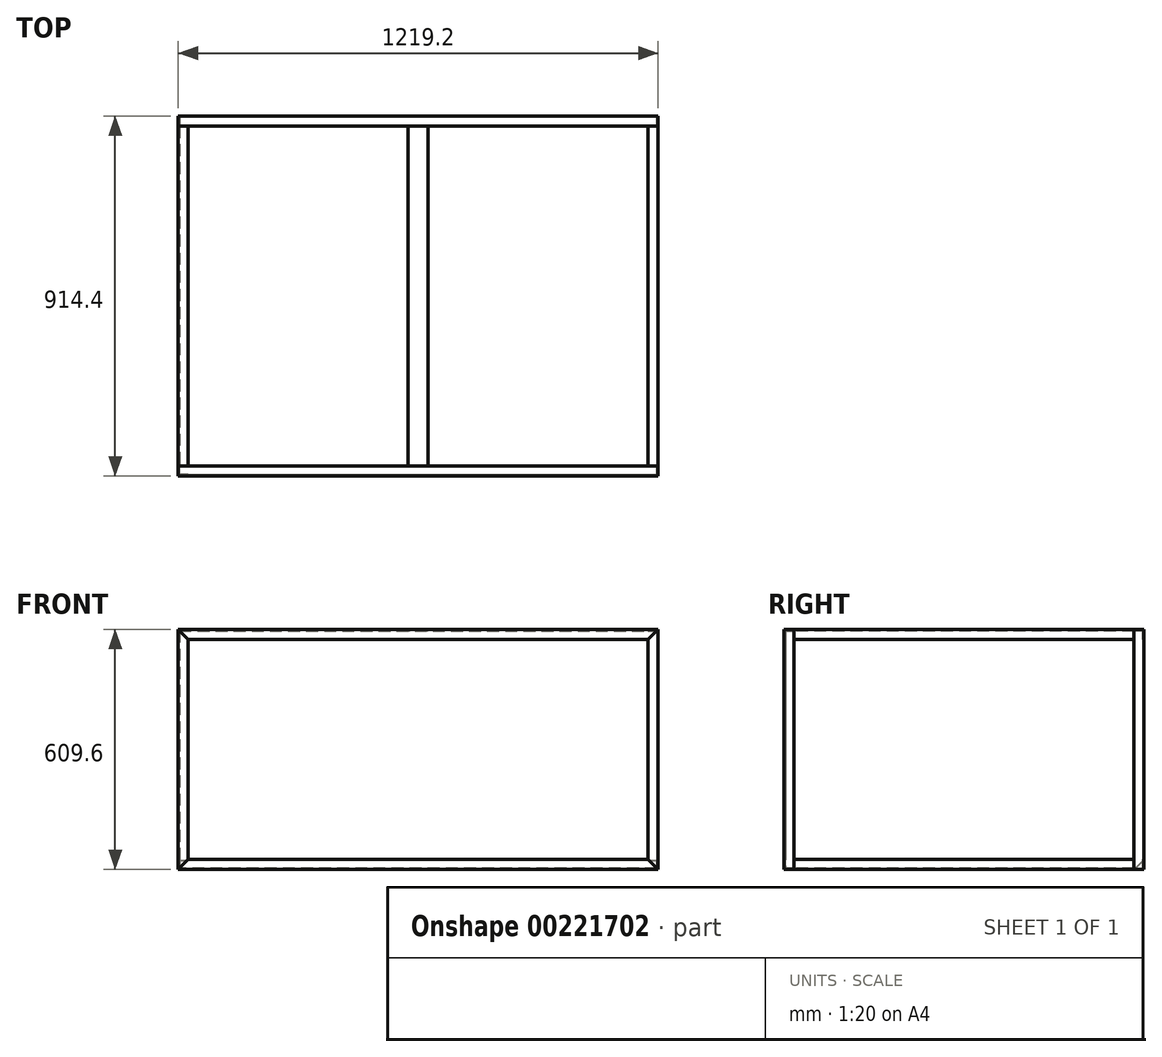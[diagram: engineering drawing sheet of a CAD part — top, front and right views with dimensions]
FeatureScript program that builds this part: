
annotation { "Feature Type Name" : "Feature", "Feature Type Description" : "" }
export const myFeature = defineFeature(function(context is Context, id is Id, definition is map)
    precondition{}
    {
        {
            var Q0;
            Q0=qCreatedBy(makeId("Top.planeOp"),FACE);
            var sketch = newSketch(context, id + "F0", { "sketchPlane" : qUnion([Q0])});
            skLineSegment(sketch, "E0", {"start": v(0, 0) * mm, "end": v(25.4, 0) * mm});
            skLineSegment(sketch, "E1", {"start": v(25.4, 0) * mm, "end": v(25.4, -3.18) * mm});
            skLineSegment(sketch, "E2", {"start": v(25.4, -3.18) * mm, "end": v(3.17, -3.18) * mm});
            skLineSegment(sketch, "E3", {"start": v(3.17, -3.18) * mm, "end": v(3.17, -25.4) * mm});
            skLineSegment(sketch, "E4", {"start": v(3.17, -25.4) * mm, "end": v(0, -25.4) * mm});
            skLineSegment(sketch, "E5", {"start": v(0, -25.4) * mm, "end": v(0, 0) * mm});
            skSolve(sketch);
        }
        {
            var Q0;
            Q0 = qSketchRegion(id + "F0", true);
            extrude(context, id + "F1", {"entities" : qUnion([Q0]), "depth" : 609.6 * mm});
        }
        {
            var Q0;
            Q0=makeQuery(id+"F1.opExtrude","SWEPT_FACE",FACE,{"disambiguationData":[OSD([sQuery(id+"F0.wireOp",EDGE,"E0")])]});
            var sketch = newSketch(context, id + "F2", { "sketchPlane" : qUnion([Q0])});
            skLineSegment(sketch, "E6", {"start": v(0, 609.6) * mm, "end": v(-25.4, 584.2) * mm});
            skLineSegment(sketch, "E7", {"start": v(-25.4, 584.2) * mm, "end": v(-25.4, 609.6) * mm});
            skLineSegment(sketch, "E8", {"start": v(-25.4, 609.6) * mm, "end": v(0, 609.6) * mm});
            skLineSegment(sketch, "E9", {"start": v(0, 0) * mm, "end": v(-25.4, 0) * mm});
            skLineSegment(sketch, "E10", {"start": v(-25.4, 0) * mm, "end": v(-25.4, 25.4) * mm});
            skLineSegment(sketch, "E11", {"start": v(-25.4, 25.4) * mm, "end": v(0, 0) * mm});
            skSolve(sketch);
        }
        {
            var Q0;
            Q0=makeQuery(id+"F2.imprint","IMPRINT",FACE,{"disambiguationData":[TD([[makeQuery(id+"F2.imprint","IMPRINT",EDGE,{"derivedFrom":sQuery(id+"F2.wireOp",EDGE,"E6")}),-1.0]])]});
            var Q1;
            Q1=makeQuery(id+"F2.imprint","IMPRINT",FACE,{"disambiguationData":[TD([[makeQuery(id+"F2.imprint","IMPRINT",EDGE,{"derivedFrom":sQuery(id+"F2.wireOp",EDGE,"E9")}),-1.0]])]});
            extrude(context, id + "F3", {"entities" : qUnion([Q0, Q1]), "operationType" : NewBodyOperationType.REMOVE, "endBound" : BoundingType.THROUGH_ALL, "oppositeDirection" : true, "depth" : 25.4 * mm});
        }
        {
            var Q0;
            Q0=makeQuery(id+"F1.opExtrude","SWEPT_BODY",BODY,{"disambiguationData":[OSD([sQuery(id+"F0.wireOp",EDGE,"E0"),sQuery(id+"F0.wireOp",EDGE,"E1"),sQuery(id+"F0.wireOp",EDGE,"E2"),sQuery(id+"F0.wireOp",EDGE,"E3"),sQuery(id+"F0.wireOp",EDGE,"E4"),sQuery(id+"F0.wireOp",EDGE,"E5")])]});
            var Q1;
            Q1=makeQuery(id+"F1.opExtrude","SWEPT_FACE",FACE,{"disambiguationData":[OSD([sQuery(id+"F0.wireOp",EDGE,"E1")])]});
            mirror(context, id + "F4", {"entities" : qUnion([Q0]), "mirrorPlane" : qUnion([Q1])});
        }
        {
            var Q0;
            Q0=makeQuery(id+"F4.opPattern","COPY",BODY,{"derivedFrom":makeQuery(id+"F1.opExtrude","SWEPT_BODY",BODY,{"disambiguationData":[OSD([sQuery(id+"F0.wireOp",EDGE,"E0"),sQuery(id+"F0.wireOp",EDGE,"E1"),sQuery(id+"F0.wireOp",EDGE,"E2"),sQuery(id+"F0.wireOp",EDGE,"E3"),sQuery(id+"F0.wireOp",EDGE,"E4"),sQuery(id+"F0.wireOp",EDGE,"E5")])]}),"instanceName":"1"});
            transform(context, id + "F5", {"entities" : qUnion([Q0]), "transformType" : TransformType.TRANSLATION_3D, "dx" : 1168.4 * mm, "dy" : 0 * mm, "dz" : 0 * mm, "makeCopy" : false});
        }
        {
            var Q0;
            Q0=qCreatedBy(makeId("Front.planeOp"),FACE);
            cPlane(context, id + "F6", {"entities" : qUnion([Q0]), "cplaneType" : CPlaneType.OFFSET, "offset" : 457.2 * mm, "width" : 152.4 * mm, "height" : 152.4 * mm});
        }
        {
            var Q0;
            Q0=makeQuery(id+"F1.opExtrude","SWEPT_BODY",BODY,{"disambiguationData":[OSD([sQuery(id+"F0.wireOp",EDGE,"E0"),sQuery(id+"F0.wireOp",EDGE,"E1"),sQuery(id+"F0.wireOp",EDGE,"E2"),sQuery(id+"F0.wireOp",EDGE,"E3"),sQuery(id+"F0.wireOp",EDGE,"E4"),sQuery(id+"F0.wireOp",EDGE,"E5")])]});
            var Q1;
            Q1=makeQuery(id+"F4.opPattern","COPY",BODY,{"derivedFrom":makeQuery(id+"F1.opExtrude","SWEPT_BODY",BODY,{"disambiguationData":[OSD([sQuery(id+"F0.wireOp",EDGE,"E0"),sQuery(id+"F0.wireOp",EDGE,"E1"),sQuery(id+"F0.wireOp",EDGE,"E2"),sQuery(id+"F0.wireOp",EDGE,"E3"),sQuery(id+"F0.wireOp",EDGE,"E4"),sQuery(id+"F0.wireOp",EDGE,"E5")])]}),"instanceName":"1"});
            var Q2;
            Q2=qCreatedBy(id+"F6.planeOp",FACE);
            mirror(context, id + "F7", {"entities" : qUnion([Q0, Q1]), "mirrorPlane" : qUnion([Q2])});
        }
        {
            var Q0;
            Q0=makeQuery(id+"F1.opExtrude","SWEPT_FACE",FACE,{"disambiguationData":[OSD([sQuery(id+"F0.wireOp",EDGE,"E5")])]});
            var sketch = newSketch(context, id + "F8", { "sketchPlane" : qUnion([Q0])});
            skLineSegment(sketch, "E12", {"start": v(25.4, 609.6) * mm, "end": v(0, 609.6) * mm});
            skLineSegment(sketch, "E13", {"start": v(0, 609.6) * mm, "end": v(0, 584.2) * mm});
            skLineSegment(sketch, "E14", {"start": v(0, 584.2) * mm, "end": v(3.17, 584.2) * mm});
            skLineSegment(sketch, "E15", {"start": v(3.17, 584.2) * mm, "end": v(3.17, 606.42) * mm});
            skLineSegment(sketch, "E16", {"start": v(3.17, 606.42) * mm, "end": v(25.4, 606.42) * mm});
            skLineSegment(sketch, "E17", {"start": v(25.4, 606.42) * mm, "end": v(25.4, 609.6) * mm});
            skLineSegment(sketch, "E18", {"start": v(25.4, 0) * mm, "end": v(0, 0) * mm});
            skLineSegment(sketch, "E19", {"start": v(0, 0) * mm, "end": v(0, 25.4) * mm});
            skLineSegment(sketch, "E20", {"start": v(0, 25.4) * mm, "end": v(25.4, 0) * mm});
            skSolve(sketch);
        }
        {
            var Q0;
            Q0 = qSketchRegion(id + "F8", true);
            var Q1;
            Q1=makeQuery(id+"F4.opPattern","COPY",FACE,{"derivedFrom":makeQuery(id+"F1.opExtrude","SWEPT_FACE",FACE,{"disambiguationData":[OSD([sQuery(id+"F0.wireOp",EDGE,"E5")])]}),"instanceName":"1"});
            extrude(context, id + "F9", {"entities" : qUnion([Q0]), "endBound" : BoundingType.UP_TO_SURFACE, "oppositeDirection" : true, "endBoundEntityFace" : qUnion([Q1]), "depth" : 25.4 * mm});
        }
        {
            var Q0;
            Q0=makeQuery(id+"F4.opPattern","COPY",BODY,{"derivedFrom":makeQuery(id+"F1.opExtrude","SWEPT_BODY",BODY,{"disambiguationData":[OSD([sQuery(id+"F0.wireOp",EDGE,"E0"),sQuery(id+"F0.wireOp",EDGE,"E1"),sQuery(id+"F0.wireOp",EDGE,"E2"),sQuery(id+"F0.wireOp",EDGE,"E3"),sQuery(id+"F0.wireOp",EDGE,"E4"),sQuery(id+"F0.wireOp",EDGE,"E5")])]}),"instanceName":"1"});
            var Q1;
            Q1=makeQuery(id+"F1.opExtrude","SWEPT_BODY",BODY,{"disambiguationData":[OSD([sQuery(id+"F0.wireOp",EDGE,"E0"),sQuery(id+"F0.wireOp",EDGE,"E1"),sQuery(id+"F0.wireOp",EDGE,"E2"),sQuery(id+"F0.wireOp",EDGE,"E3"),sQuery(id+"F0.wireOp",EDGE,"E4"),sQuery(id+"F0.wireOp",EDGE,"E5")])]});
            var Q2;
            Q2=makeQuery(id+"F9.opExtrude","SWEPT_BODY",BODY,{"disambiguationData":[OSD([sQuery(id+"F8.wireOp",EDGE,"E12"),sQuery(id+"F8.wireOp",EDGE,"E13"),sQuery(id+"F8.wireOp",EDGE,"E14"),sQuery(id+"F8.wireOp",EDGE,"E15"),sQuery(id+"F8.wireOp",EDGE,"E16"),sQuery(id+"F8.wireOp",EDGE,"E17")])]});
            var Q3;
            Q3=makeQuery(id+"F9.opExtrude","SWEPT_BODY",BODY,{"disambiguationData":[OSD([sQuery(id+"F8.wireOp",EDGE,"E18"),sQuery(id+"F8.wireOp",EDGE,"E19"),sQuery(id+"F8.wireOp",EDGE,"E20")])]});
            booleanBodies(context, id + "F10", {"operationType" : BooleanOperationType.SUBTRACTION, "tools" : qUnion([Q0, Q1]), "targets" : qUnion([Q2, Q3]), "keepTools" : true});
        }
        {
            var Q0;
            Q0=makeQuery(id+"F7.opPattern","COPY",FACE,{"derivedFrom":makeQuery(id+"F1.opExtrude","SWEPT_FACE",FACE,{"disambiguationData":[OSD([sQuery(id+"F0.wireOp",EDGE,"E5")])]}),"instanceName":"1"});
            var sketch = newSketch(context, id + "F11", { "sketchPlane" : qUnion([Q0])});
            skLineSegment(sketch, "E21", {"start": v(889, 0) * mm, "end": v(914.4, 0) * mm});
            skLineSegment(sketch, "E22", {"start": v(914.4, 0) * mm, "end": v(914.4, 25.4) * mm});
            skLineSegment(sketch, "E23", {"start": v(889, 609.6) * mm, "end": v(914.4, 609.6) * mm});
            skLineSegment(sketch, "E24", {"start": v(914.4, 609.6) * mm, "end": v(914.4, 584.2) * mm});
            skLineSegment(sketch, "E25", {"start": v(914.4, 25.4) * mm, "end": v(911.23, 25.4) * mm});
            skLineSegment(sketch, "E26", {"start": v(911.23, 25.4) * mm, "end": v(911.23, 3.18) * mm});
            skLineSegment(sketch, "E27", {"start": v(911.23, 3.18) * mm, "end": v(889, 3.17) * mm});
            skLineSegment(sketch, "E28", {"start": v(889, 3.17) * mm, "end": v(889, 0) * mm});
            skLineSegment(sketch, "E29", {"start": v(889, 609.6) * mm, "end": v(889, 606.42) * mm});
            skLineSegment(sketch, "E30", {"start": v(889, 606.42) * mm, "end": v(911.23, 606.42) * mm});
            skLineSegment(sketch, "E31", {"start": v(911.23, 606.42) * mm, "end": v(911.23, 584.2) * mm});
            skLineSegment(sketch, "E32", {"start": v(911.23, 584.2) * mm, "end": v(914.4, 584.2) * mm});
            skSolve(sketch);
        }
        {
            var Q0;
            Q0 = qSketchRegion(id + "F11", true);
            var Q1;
            Q1=makeQuery(id+"F7.opPattern","COPY",FACE,{"derivedFrom":makeQuery(id+"F4.opPattern","COPY",FACE,{"derivedFrom":makeQuery(id+"F1.opExtrude","SWEPT_FACE",FACE,{"disambiguationData":[OSD([sQuery(id+"F0.wireOp",EDGE,"E5")])]}),"instanceName":"1"}),"instanceName":"1"});
            extrude(context, id + "F12", {"entities" : qUnion([Q0]), "endBound" : BoundingType.UP_TO_SURFACE, "oppositeDirection" : true, "endBoundEntityFace" : qUnion([Q1]), "depth" : 25.4 * mm});
        }
        {
            var Q0;
            Q0=makeQuery(id+"F7.opPattern","COPY",BODY,{"derivedFrom":makeQuery(id+"F1.opExtrude","SWEPT_BODY",BODY,{"disambiguationData":[OSD([sQuery(id+"F0.wireOp",EDGE,"E0"),sQuery(id+"F0.wireOp",EDGE,"E1"),sQuery(id+"F0.wireOp",EDGE,"E2"),sQuery(id+"F0.wireOp",EDGE,"E3"),sQuery(id+"F0.wireOp",EDGE,"E4"),sQuery(id+"F0.wireOp",EDGE,"E5")])]}),"instanceName":"1"});
            var Q1;
            Q1=makeQuery(id+"F7.opPattern","COPY",BODY,{"derivedFrom":makeQuery(id+"F4.opPattern","COPY",BODY,{"derivedFrom":makeQuery(id+"F1.opExtrude","SWEPT_BODY",BODY,{"disambiguationData":[OSD([sQuery(id+"F0.wireOp",EDGE,"E0"),sQuery(id+"F0.wireOp",EDGE,"E1"),sQuery(id+"F0.wireOp",EDGE,"E2"),sQuery(id+"F0.wireOp",EDGE,"E3"),sQuery(id+"F0.wireOp",EDGE,"E4"),sQuery(id+"F0.wireOp",EDGE,"E5")])]}),"instanceName":"1"}),"instanceName":"1"});
            var Q2;
            Q2=makeQuery(id+"F12.opExtrude","SWEPT_BODY",BODY,{"disambiguationData":[OSD([sQuery(id+"F11.wireOp",EDGE,"E23"),sQuery(id+"F11.wireOp",EDGE,"E24"),sQuery(id+"F11.wireOp",EDGE,"E29"),sQuery(id+"F11.wireOp",EDGE,"E30"),sQuery(id+"F11.wireOp",EDGE,"E31"),sQuery(id+"F11.wireOp",EDGE,"E32")])]});
            var Q3;
            Q3=makeQuery(id+"F12.opExtrude","SWEPT_BODY",BODY,{"disambiguationData":[OSD([sQuery(id+"F11.wireOp",EDGE,"E21"),sQuery(id+"F11.wireOp",EDGE,"E22"),sQuery(id+"F11.wireOp",EDGE,"E25"),sQuery(id+"F11.wireOp",EDGE,"E26"),sQuery(id+"F11.wireOp",EDGE,"E27"),sQuery(id+"F11.wireOp",EDGE,"E28")])]});
            booleanBodies(context, id + "F13", {"operationType" : BooleanOperationType.SUBTRACTION, "tools" : qUnion([Q0, Q1]), "targets" : qUnion([Q2, Q3]), "keepTools" : true});
        }
        {
            var Q0;
            Q0=makeQuery(id+"F7.opPattern","COPY",FACE,{"derivedFrom":makeQuery(id+"F4.opPattern","COPY",FACE,{"derivedFrom":makeQuery(id+"F1.opExtrude","SWEPT_FACE",FACE,{"disambiguationData":[OSD([sQuery(id+"F0.wireOp",EDGE,"E5")])]}),"instanceName":"1"}),"instanceName":"1"});
            var sketch = newSketch(context, id + "F14", { "sketchPlane" : qUnion([Q0])});
            skLineSegment(sketch, "E33", {"start": v(-889, 609.6) * mm, "end": v(-914.4, 609.6) * mm});
            skLineSegment(sketch, "E34", {"start": v(-914.4, 609.6) * mm, "end": v(-914.4, 584.2) * mm});
            skLineSegment(sketch, "E35", {"start": v(-914.4, 584.2) * mm, "end": v(-911.22, 584.2) * mm});
            skLineSegment(sketch, "E36", {"start": v(-911.22, 584.2) * mm, "end": v(-911.22, 606.43) * mm});
            skLineSegment(sketch, "E37", {"start": v(-911.22, 606.43) * mm, "end": v(-889, 606.43) * mm});
            skLineSegment(sketch, "E38", {"start": v(-889, 606.43) * mm, "end": v(-889, 609.6) * mm});
            skSolve(sketch);
        }
        {
            var Q0;
            Q0 = qSketchRegion(id + "F14", true);
            var Q1;
            Q1=makeQuery(id+"F7.opPattern","COPY",FACE,{"derivedFrom":makeQuery(id+"F1.opExtrude","SWEPT_FACE",FACE,{"disambiguationData":[OSD([sQuery(id+"F0.wireOp",EDGE,"E5")])]}),"instanceName":"1"});
            extrude(context, id + "F15", {"entities" : qUnion([Q0]), "endBound" : BoundingType.UP_TO_SURFACE, "oppositeDirection" : true, "endBoundEntityFace" : qUnion([Q1]), "depth" : 25.4 * mm});
        }
        {
            var Q0;
            Q0=makeQuery(id+"F7.opPattern","COPY",BODY,{"derivedFrom":makeQuery(id+"F4.opPattern","COPY",BODY,{"derivedFrom":makeQuery(id+"F1.opExtrude","SWEPT_BODY",BODY,{"disambiguationData":[OSD([sQuery(id+"F0.wireOp",EDGE,"E0"),sQuery(id+"F0.wireOp",EDGE,"E1"),sQuery(id+"F0.wireOp",EDGE,"E2"),sQuery(id+"F0.wireOp",EDGE,"E3"),sQuery(id+"F0.wireOp",EDGE,"E4"),sQuery(id+"F0.wireOp",EDGE,"E5")])]}),"instanceName":"1"}),"instanceName":"1"});
            var Q1;
            Q1=makeQuery(id+"F7.opPattern","COPY",BODY,{"derivedFrom":makeQuery(id+"F1.opExtrude","SWEPT_BODY",BODY,{"disambiguationData":[OSD([sQuery(id+"F0.wireOp",EDGE,"E0"),sQuery(id+"F0.wireOp",EDGE,"E1"),sQuery(id+"F0.wireOp",EDGE,"E2"),sQuery(id+"F0.wireOp",EDGE,"E3"),sQuery(id+"F0.wireOp",EDGE,"E4"),sQuery(id+"F0.wireOp",EDGE,"E5")])]}),"instanceName":"1"});
            var Q2;
            Q2=makeQuery(id+"F15.opExtrude","SWEPT_BODY",BODY,{"disambiguationData":[OSD([sQuery(id+"F14.wireOp",EDGE,"E33"),sQuery(id+"F14.wireOp",EDGE,"E34"),sQuery(id+"F14.wireOp",EDGE,"E35"),sQuery(id+"F14.wireOp",EDGE,"E36"),sQuery(id+"F14.wireOp",EDGE,"E37"),sQuery(id+"F14.wireOp",EDGE,"E38")])]});
            booleanBodies(context, id + "F16", {"operationType" : BooleanOperationType.SUBTRACTION, "tools" : qUnion([Q0, Q1]), "targets" : qUnion([Q2]), "keepTools" : true});
        }
        {
            var Q0;
            Q0=makeQuery(id+"F12.opExtrude","SWEPT_FACE",FACE,{"disambiguationData":[OSD([sQuery(id+"F11.wireOp",EDGE,"E29")])]});
            var sketch = newSketch(context, id + "F17", { "sketchPlane" : qUnion([Q0])});
            skLineSegment(sketch, "E39", {"start": v(-25.4, 609.6) * mm, "end": v(0, 609.6) * mm});
            skLineSegment(sketch, "E40", {"start": v(0, 609.6) * mm, "end": v(0, 584.2) * mm});
            skLineSegment(sketch, "E41", {"start": v(0, 584.2) * mm, "end": v(-3.18, 584.2) * mm});
            skLineSegment(sketch, "E42", {"start": v(-3.18, 584.2) * mm, "end": v(-3.18, 606.42) * mm});
            skLineSegment(sketch, "E43", {"start": v(-3.18, 606.42) * mm, "end": v(-25.4, 606.42) * mm});
            skLineSegment(sketch, "E44", {"start": v(-25.4, 606.42) * mm, "end": v(-25.4, 609.6) * mm});
            skLineSegment(sketch, "E45", {"start": v(-1193.8, 609.6) * mm, "end": v(-1219.2, 609.6) * mm});
            skLineSegment(sketch, "E46", {"start": v(-1219.2, 609.6) * mm, "end": v(-1219.2, 584.2) * mm});
            skLineSegment(sketch, "E47", {"start": v(-1219.2, 584.2) * mm, "end": v(-1216.03, 584.2) * mm});
            skLineSegment(sketch, "E48", {"start": v(-1216.03, 584.2) * mm, "end": v(-1216.03, 606.42) * mm});
            skLineSegment(sketch, "E49", {"start": v(-1216.03, 606.42) * mm, "end": v(-1193.8, 606.42) * mm});
            skLineSegment(sketch, "E50", {"start": v(-1193.8, 606.42) * mm, "end": v(-1193.8, 609.6) * mm});
            skLineSegment(sketch, "E51", {"start": v(-1219.2, 0) * mm, "end": v(-1193.8, 0) * mm});
            skLineSegment(sketch, "E52", {"start": v(-1193.8, 0) * mm, "end": v(-1193.8, 3.17) * mm});
            skLineSegment(sketch, "E53", {"start": v(-1193.8, 3.17) * mm, "end": v(-1216.03, 3.17) * mm});
            skLineSegment(sketch, "E54", {"start": v(-1216.03, 3.17) * mm, "end": v(-1216.03, 25.4) * mm});
            skLineSegment(sketch, "E55", {"start": v(-1216.03, 25.4) * mm, "end": v(-1219.2, 25.4) * mm});
            skLineSegment(sketch, "E56", {"start": v(-1219.2, 25.4) * mm, "end": v(-1219.2, 0) * mm});
            skLineSegment(sketch, "E57", {"start": v(0, 0) * mm, "end": v(-25.4, 0) * mm});
            skLineSegment(sketch, "E58", {"start": v(-25.4, 0) * mm, "end": v(-25.4, 3.17) * mm});
            skLineSegment(sketch, "E59", {"start": v(-25.4, 3.17) * mm, "end": v(-3.17, 3.17) * mm});
            skLineSegment(sketch, "E60", {"start": v(-3.17, 3.18) * mm, "end": v(-3.18, 25.4) * mm});
            skLineSegment(sketch, "E61", {"start": v(-3.18, 25.4) * mm, "end": v(0, 25.4) * mm});
            skLineSegment(sketch, "E62", {"start": v(0, 25.4) * mm, "end": v(0, 0) * mm});
            skSolve(sketch);
        }
        {
            var Q0;
            Q0 = qSketchRegion(id + "F17", true);
            var Q1;
            Q1=makeQuery(id+"F1.opExtrude","SWEPT_FACE",FACE,{"disambiguationData":[OSD([sQuery(id+"F0.wireOp",EDGE,"E4")])]});
            extrude(context, id + "F18", {"entities" : qUnion([Q0]), "endBound" : BoundingType.UP_TO_SURFACE, "endBoundEntityFace" : qUnion([Q1]), "depth" : 25.4 * mm});
        }
        {
            var Q0;
            Q0=makeQuery(id+"F9.opExtrude","SWEPT_FACE",FACE,{"disambiguationData":[OSD([sQuery(id+"F8.wireOp",EDGE,"E12")])]});
            var sketch = newSketch(context, id + "F19", { "sketchPlane" : qUnion([Q0])});
            skLineSegment(sketch, "E63", {"start": v(609.6, -25.4) * mm, "end": v(635, -25.4) * mm});
            skLineSegment(sketch, "E64", {"start": v(635, -25.4) * mm, "end": v(635, -889) * mm});
            skLineSegment(sketch, "E65", {"start": v(635, -889) * mm, "end": v(584.2, -889) * mm});
            skLineSegment(sketch, "E66", {"start": v(584.2, -889) * mm, "end": v(584.2, -25.4) * mm});
            skLineSegment(sketch, "E67", {"start": v(584.2, -25.4) * mm, "end": v(609.6, -25.4) * mm});
            skLineSegment(sketch, "E68.0", {"start": v(1219.2, -889) * mm, "end": v(0, -889) * mm, "construction": true});
            skSolve(sketch);
        }
        {
            var Q0;
            Q0=makeQuery(id+"F19.imprint","IMPRINT",FACE,{"disambiguationData":[TD([[makeQuery(id+"F19.imprint","IMPRINT",EDGE,{"derivedFrom":sQuery(id+"F19.wireOp",EDGE,"E63")}),1.0]])]});
            var Q1;
            Q1=makeQuery(id+"F12.opExtrude","SWEPT_FACE",FACE,{"disambiguationData":[OSD([sQuery(id+"F11.wireOp",EDGE,"E30")])]});
            extrude(context, id + "F20", {"entities" : qUnion([Q0]), "endBound" : BoundingType.UP_TO_SURFACE, "oppositeDirection" : true, "endBoundEntityFace" : qUnion([Q1]), "depth" : 25.4 * mm});
        }
    });
